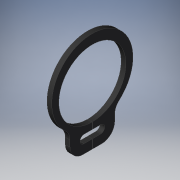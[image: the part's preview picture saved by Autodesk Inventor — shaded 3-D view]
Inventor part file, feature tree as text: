
AUTODESK INVENTOR PART (.ipt)
format: ipt  version: 2019 (Build 230136000, 136)  size: 152,576 bytes
history: native  units: mm
features: other x14, extrude x1, sketch x1
ambient origin geometry x8: Origin, YZ Plane, XZ Plane, XY Plane, X Axis, Y Axis, Z Axis, Center Point
bodies: Solid1 (feature_tree)
feature tree (16):
  extrude  "Extrusion1"  TaperAngle=0.0deg  [1 undecoded]
  other  "1_XY"
  other  "1_YZ"
  other  "1_ZX"
  other  "1_X"
  other  "1_Y"
  other  "1_Z"
  other  "1_Center"
  other  "combination_module_XY"
  other  "combination_module_YZ"
  other  "combination_module_ZX"
  other  "combination_module_X"
  other  "combination_module_Y"
  other  "combination_module_Z"
  other  "combination_module_Center"
  sketch  "Sketch_5"  dims[d0=0.4mm d1=0.0mm d2=0.0mm]
note: 1 required parameter value undecoded (feature->parameter linkage not recoverable at this tier; creation-order binding heuristic only, values carry confidence <= 0.55)
